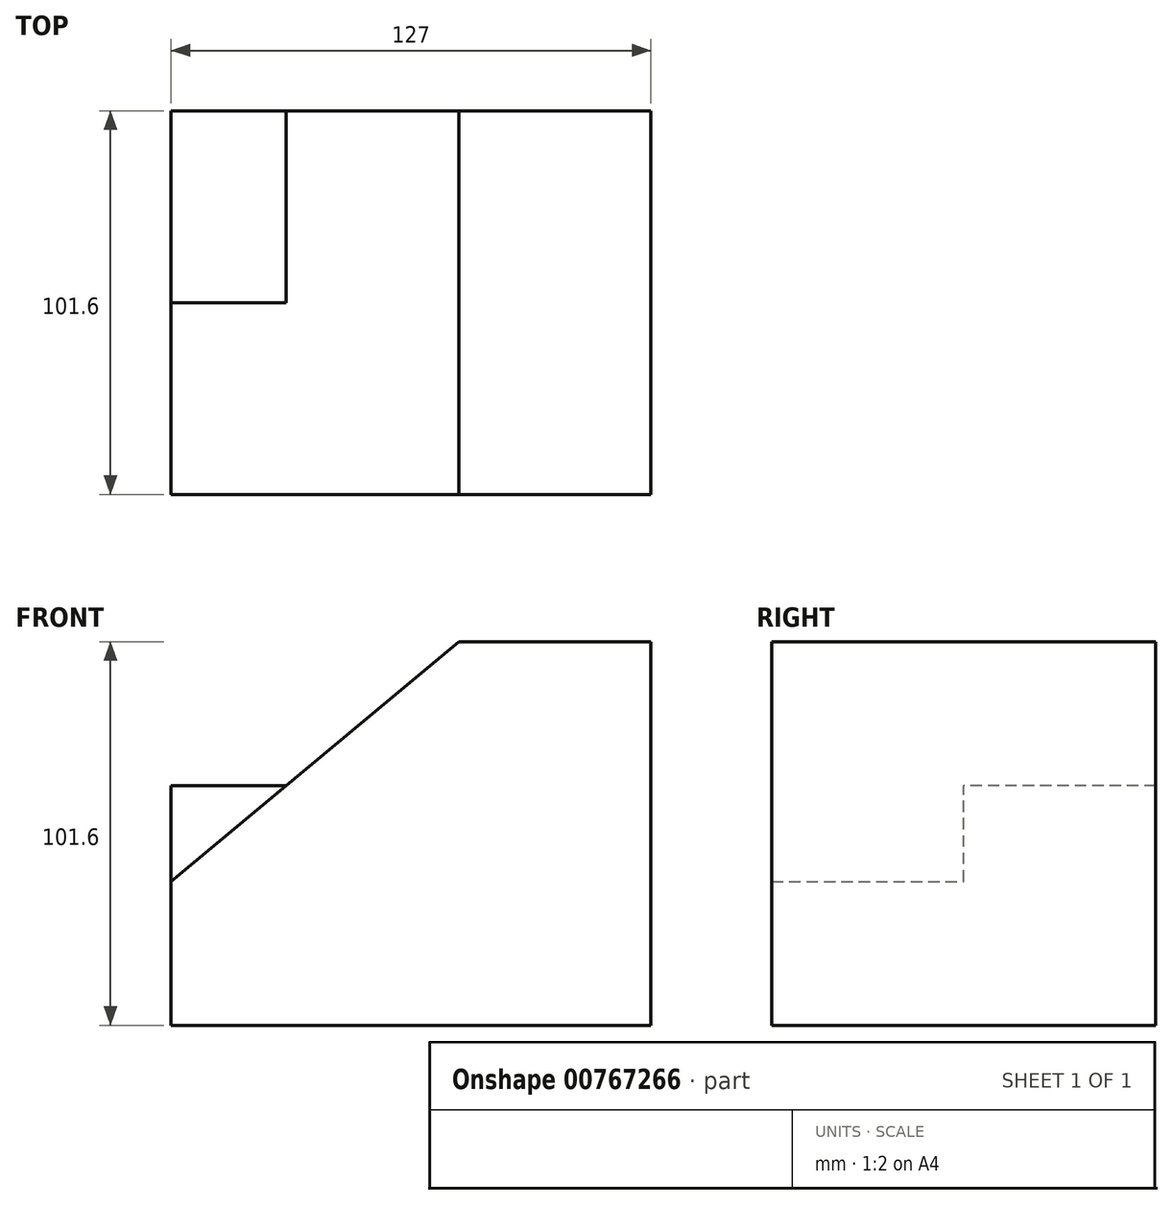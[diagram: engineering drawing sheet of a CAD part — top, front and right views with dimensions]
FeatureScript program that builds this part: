
annotation { "Feature Type Name" : "Feature", "Feature Type Description" : "" }
export const myFeature = defineFeature(function(context is Context, id is Id, definition is map)
    precondition{}
    {
        {
            var Q0;
            Q0=qCreatedBy(makeId("Front.planeOp"),FACE);
            var sketch = newSketch(context, id + "F0", { "sketchPlane" : qUnion([Q0])});
            skLineSegment(sketch, "E0.bottom", {"start": v(33.03, 38.1) * mm, "end": v(83.83, 38.1) * mm});
            skLineSegment(sketch, "E0.top", {"start": v(33.03, -63.5) * mm, "end": v(83.83, -63.5) * mm});
            skLineSegment(sketch, "E0.left", {"start": v(33.03, 38.1) * mm, "end": v(33.03, -63.5) * mm});
            skLineSegment(sketch, "E0.right", {"start": v(83.83, 38.1) * mm, "end": v(83.83, -63.5) * mm});
            skLineSegment(sketch, "E1", {"start": v(33.03, -63.5) * mm, "end": v(-43.17, -63.5) * mm});
            skLineSegment(sketch, "E2", {"start": v(-43.17, -63.5) * mm, "end": v(-43.17, -25.4) * mm});
            skLineSegment(sketch, "E3", {"start": v(-43.17, -25.4) * mm, "end": v(33.03, 38.1) * mm});
            skLineSegment(sketch, "E4", {"start": v(-43.17, -25.4) * mm, "end": v(-43.17, 0) * mm});
            skLineSegment(sketch, "E5", {"start": v(-43.17, 0) * mm, "end": v(0, 0) * mm});
            skSolve(sketch);
        }
        {
            var Q0;
            Q0=makeQuery(id+"F0.imprint","IMPRINT",FACE,{"disambiguationData":[TD([[makeQuery(id+"F0.imprint","IMPRINT",EDGE,{"derivedFrom":sQuery(id+"F0.wireOp",EDGE,"E0.bottom")}),-1.0]])]});
            var Q1;
            {var subQ3=sQuery(id+"F0.wireOp",EDGE,"E0.left");Q1=makeQuery(id+"F0.imprint","IMPRINT",FACE,{"disambiguationData":[TD([[makeQuery(id+"F0.imprint","IMPRINT",EDGE,{"derivedFrom":subQ3}),-1.0]])]});}
            extrude(context, id + "F1", {"entities" : qUnion([Q0, Q1]), "endBound" : BoundingType.SYMMETRIC, "depth" : 101.6 * mm, "offsetDistance" : 25.4 * mm});
        }
        {
            var Q0;
            {var subQ0=sQuery(id+"F0.wireOp",EDGE,"E4");Q0=makeQuery(id+"F0.imprint","IMPRINT",FACE,{"disambiguationData":[TD([[makeQuery(id+"F0.imprint","IMPRINT",EDGE,{"derivedFrom":subQ0}),-1.0]])]});}
            extrude(context, id + "F2", {"entities" : qUnion([Q0]), "operationType" : NewBodyOperationType.ADD, "oppositeDirection" : true, "depth" : 50.8 * mm, "offsetDistance" : 25.4 * mm});
        }
    });
